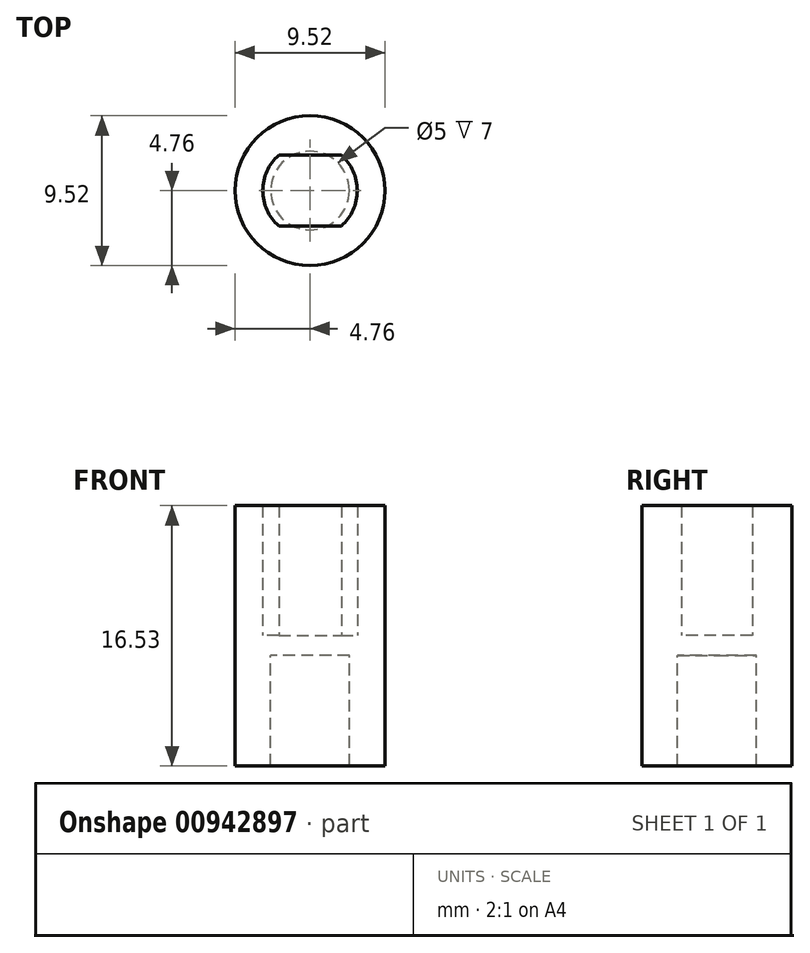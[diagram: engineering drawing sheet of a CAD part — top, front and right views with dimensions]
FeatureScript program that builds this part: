
annotation { "Feature Type Name" : "Feature", "Feature Type Description" : "" }
export const myFeature = defineFeature(function(context is Context, id is Id, definition is map)
    precondition{}
    {
        {
            var Q0;
            Q0=qCreatedBy(makeId("Top.planeOp"),FACE);
            var sketch = newSketch(context, id + "F0", { "sketchPlane" : qUnion([Q0])});
            skCircle(sketch, "E0", {"center": v(0, 0) * mm, "radius": 4.76 * mm});
            skSolve(sketch);
        }
        {
            var Q0;
            Q0=qSketchRegion(id+"F0",true);
            extrude(context, id + "F1", {"entities" : qUnion([Q0]), "depth" : 9.52 * mm, "offsetDistance" : 25.4 * mm, "hasSecondDirection" : true, "secondDirectionOppositeDirection" : true, "secondDirectionDepth" : 7 * mm});
        }
        {
            var Q0;
            Q0=qCreatedBy(makeId("Top.planeOp"),FACE);
            var sketch = newSketch(context, id + "F2", { "sketchPlane" : qUnion([Q0])});
            skCircle(sketch, "E1", {"center": v(0, 0) * mm, "radius": 3 * mm});
            skLineSegment(sketch, "E2", {"start": v(-1.98, 2.25) * mm, "end": v(1.98, 2.25) * mm});
            skLineSegment(sketch, "E3", {"start": v(-1.98, -2.25) * mm, "end": v(1.98, -2.25) * mm});
            skSolve(sketch);
        }
        {
            var Q0;
            Q0=qCreatedBy(makeId("Top.planeOp"),FACE);
            var sketch = newSketch(context, id + "F3", { "sketchPlane" : qUnion([Q0])});
            skCircle(sketch, "E4", {"center": v(0, 0) * mm, "radius": 2.5 * mm});
            skSolve(sketch);
        }
        {
            var Q0;
            {var subQ0=sQuery(id+"F2.wireOp",EDGE,"E2");Q0=makeQuery(id+"F2.imprint","IMPRINT",FACE,{"disambiguationData":[TD([[makeQuery(id+"F2.imprint","IMPRINT",EDGE,{"derivedFrom":subQ0}),-1.0]])]});}
            extrude(context, id + "F4", {"entities" : qUnion([Q0]), "operationType" : NewBodyOperationType.REMOVE, "endBound" : BoundingType.THROUGH_ALL, "depth" : 25.4 * mm, "offsetDistance" : 25.4 * mm});
        }
        {
            var Q0;
            Q0=qSketchRegion(id+"F3",true);
            extrude(context, id + "F5", {"entities" : qUnion([Q0]), "operationType" : NewBodyOperationType.REMOVE, "endBound" : BoundingType.THROUGH_ALL, "oppositeDirection" : true, "depth" : 25.4 * mm, "offsetDistance" : 25.4 * mm});
        }
        {
            var Q0;
            Q0=qSketchRegion(id+"F0",true);
            extrude(context, id + "F6", {"entities" : qUnion([Q0]), "operationType" : NewBodyOperationType.ADD, "depth" : 1.27 * mm, "offsetDistance" : 25.4 * mm});
        }
    });
